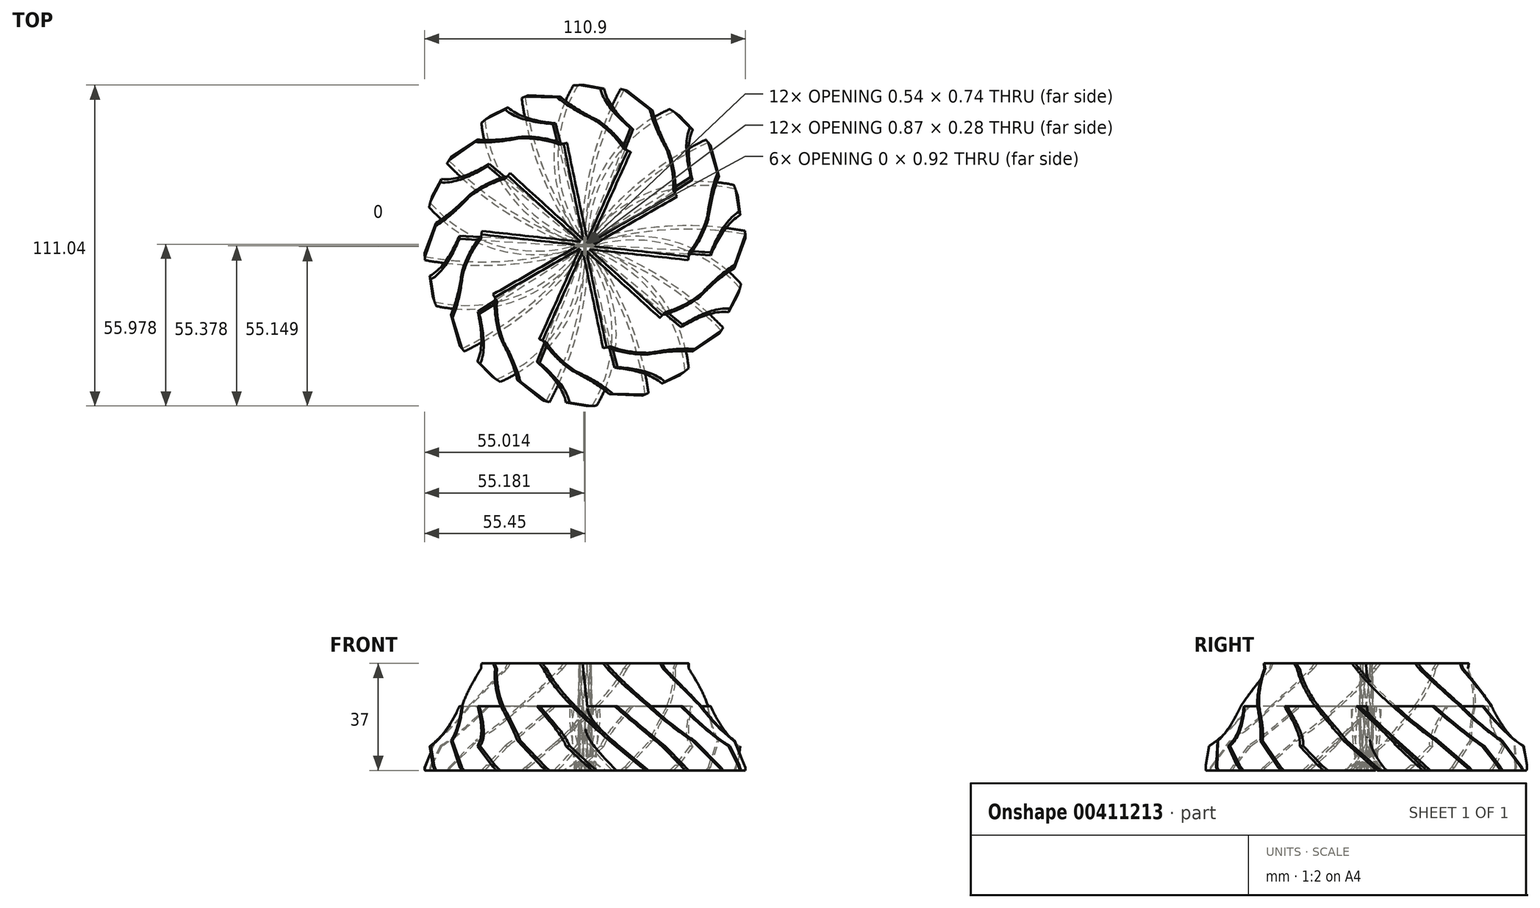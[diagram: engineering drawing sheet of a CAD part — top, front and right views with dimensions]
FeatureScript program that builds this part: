
annotation { "Feature Type Name" : "Feature", "Feature Type Description" : "" }
export const myFeature = defineFeature(function(context is Context, id is Id, definition is map)
    precondition{}
    {
        {
            var Q0;
            Q0=qCreatedBy(makeId("Front.planeOp"),FACE);
            var sketch = newSketch(context, id + "F0", { "sketchPlane" : qUnion([Q0])});
            skLineSegment(sketch, "E0", {"start": v(0, 70) * mm, "end": v(0, -70) * mm, "construction": true});
            skLineSegment(sketch, "E1", {"start": v(0, 0) * mm, "end": v(56, 0) * mm});
            skLineSegment(sketch, "E2", {"start": v(56, 0) * mm, "end": v(56, 1.8) * mm});
            skLineSegment(sketch, "E3", {"start": v(0, 38.2) * mm, "end": v(16, 38.2) * mm});
            skArc(sketch, "E4", {"start": v(16, 38.2) * mm, "mid": v(28.5, 11.77) * mm, "end": v(56, 1.8) * mm});
            skLineSegment(sketch, "E5", {"start": v(16, 0) * mm, "end": v(36, 0) * mm, "construction": true});
            skSolve(sketch);
        }
        {
            var Q0;
            Q0=sQuery(id+"F0.wireOp",EDGE,"E1");
            var Q1;
            Q1=sQuery(id+"F0.wireOp",EDGE,"E4");
            var Q2;
            Q2=sQuery(id+"F0.wireOp",EDGE,"E3");
            var Q3;
            Q3=sQuery(id+"F0.wireOp",EDGE,"E2");
            var Q4;
            Q4=sQuery(id+"F0.wireOp",EDGE,"E0");
            revolve(context, id + "F1", {"bodyType" : ToolBodyType.SURFACE, "surfaceOperationType" : NewSurfaceOperationType.NEW, "surfaceEntities" : qUnion([Q0, Q1, Q2, Q3]), "axis" : qUnion([Q4]), "revolveType" : RevolveType.FULL});
        }
        {
            var Q0;
            Q0=makeQuery(id+"F1.opRevolve","SWEPT_FACE",FACE,{"disambiguationData":[OSD([sQuery(id+"F0.wireOp",EDGE,"E3")])]});
            cPlane(context, id + "F2", {"entities" : qUnion([Q0]), "cplaneType" : CPlaneType.OFFSET, "offset" : (0) * mm, "width" : 150 * mm, "height" : 150 * mm});
        }
        {
            var Q0;
            Q0=qCreatedBy(makeId("Top.planeOp"),FACE);
            var sketch = newSketch(context, id + "F3", { "sketchPlane" : qUnion([Q0])});
            skArc(sketch, "E6", {"start": v(43, 35.88) * mm, "mid": v(19.23, 20.65) * mm, "end": v(0, 0) * mm});
            skArc(sketch, "E7.0", {"start": v(42.2, 36.82) * mm, "mid": v(18.98, 22) * mm, "end": v(0, 2.03) * mm});
            skLineSegment(sketch, "E8", {"start": v(0, 0) * mm, "end": v(0, 2.03) * mm});
            skLineSegment(sketch, "E9", {"start": v(43, 35.88) * mm, "end": v(42.2, 36.82) * mm});
            skSolve(sketch);
        }
        {
            var Q0;
            Q0=qCreatedBy(id+"F2.planeOp",FACE);
            var sketch = newSketch(context, id + "F4", { "sketchPlane" : qUnion([Q0])});
            skLineSegment(sketch, "E10", {"start": v(0, 0) * mm, "end": v(55.5, -7.44) * mm});
            skLineSegment(sketch, "E11", {"start": v(55.5, -7.44) * mm, "end": v(55.34, -8.63) * mm});
            skLineSegment(sketch, "E12", {"start": v(55.34, -8.63) * mm, "end": v(0, -1.21) * mm});
            skLineSegment(sketch, "E13", {"start": v(0, -1.21) * mm, "end": v(0, 0) * mm});
            skLineSegment(sketch, "E14", {"start": v(47.95, -28.93) * mm, "end": v(13.75, -8.3) * mm});
            skLineSegment(sketch, "E15", {"start": v(13.75, -8.3) * mm, "end": v(13.23, -9.15) * mm});
            skLineSegment(sketch, "E16", {"start": v(13.23, -9.15) * mm, "end": v(47.48, -29.81) * mm});
            skLineSegment(sketch, "E17", {"start": v(47.48, -29.81) * mm, "end": v(47.95, -28.93) * mm});
            skCircle(sketch, "E18", {"center": v(55.5, -7.44) * mm, "radius": 22.78 * mm, "construction": true});
            skSolve(sketch);
        }
        {
            var Q0;
            Q0=makeQuery(id+"F1.opRevolve","SWEPT_FACE",FACE,{"disambiguationData":[OSD([sQuery(id+"F0.wireOp",EDGE,"E3")])]});
            cPlane(context, id + "F5", {"entities" : qUnion([Q0]), "cplaneType" : CPlaneType.OFFSET, "offset" : 16 * mm, "oppositeDirection" : true, "width" : 150 * mm, "height" : 150 * mm});
        }
        {
            var Q0;
            Q0=qCreatedBy(makeId("Top.planeOp"),FACE);
            var sketch = newSketch(context, id + "F6", { "sketchPlane" : qUnion([Q0])});
            skArc(sketch, "E19", {"start": v(29.73, 47.35) * mm, "mid": v(7.41, 28.35) * mm, "end": v(0, 0) * mm});
            skLineSegment(sketch, "E20", {"start": v(0, 0) * mm, "end": v(1, 0) * mm});
            skArc(sketch, "E21", {"start": v(31.03, 46.53) * mm, "mid": v(8.78, 27.93) * mm, "end": v(1, 0) * mm});
            skLineSegment(sketch, "E22", {"start": v(29.73, 47.35) * mm, "end": v(31.03, 46.53) * mm});
            skSolve(sketch);
        }
        {
            var Q0;
            Q0=qCreatedBy(id+"F5.planeOp",FACE);
            var sketch = newSketch(context, id + "F7", { "sketchPlane" : qUnion([Q0])});
            skLineSegment(sketch, "E23", {"start": v(1.07, 0) * mm, "end": v(47.4, 29.32) * mm});
            skLineSegment(sketch, "E24", {"start": v(47.4, 29.32) * mm, "end": v(46.88, 30.16) * mm});
            skLineSegment(sketch, "E25", {"start": v(46.88, 30.16) * mm, "end": v(0, 0.5) * mm});
            skLineSegment(sketch, "E26", {"start": v(0, 0.5) * mm, "end": v(1.07, 0) * mm});
            skSolve(sketch);
        }
        {
            var Q0;
            Q0 = qSketchRegion(id + "F3", true);
            var Q1;
            Q1=makeQuery(id+"F4.imprint","IMPRINT",FACE,{"disambiguationData":[TD([[makeQuery(id+"F4.imprint","IMPRINT",EDGE,{"derivedFrom":sQuery(id+"F4.wireOp",EDGE,"E10")}),-1.0]])]});
            loft(context, id + "F8", {"sheetProfilesArray" : [{ "sheetProfileEntities" : qUnion([Q0]) }, { "sheetProfileEntities" : qUnion([Q1]) }]});
        }
        {
            var Q0;
            Q0 = qSketchRegion(id + "F7", true);
            var Q1;
            Q1 = qSketchRegion(id + "F6", true);
            loft(context, id + "F9", {"sheetProfilesArray" : [{ "sheetProfileEntities" : qUnion([Q0]) }, { "sheetProfileEntities" : qUnion([Q1]) }]});
        }
        {
            var Q0;
            Q0=makeQuery(id+"F8.opLoft","SWEPT_BODY",BODY,{"disambiguationData":[OSD([makeQuery(id+"F3.imprint","IMPRINT",FACE,{"disambiguationData":[TD([[makeQuery(id+"F3.imprint","IMPRINT",EDGE,{"derivedFrom":sQuery(id+"F3.wireOp",EDGE,"E6")}),-1.0]])]}),makeQuery(id+"F4.imprint","IMPRINT",FACE,{"disambiguationData":[TD([[makeQuery(id+"F4.imprint","IMPRINT",EDGE,{"derivedFrom":sQuery(id+"F4.wireOp",EDGE,"20717ec0-5c2d-4e27-b742-bf9efb357e74")}),-1.0]])]})])]});
            var Q1;
            Q1=makeQuery(id+"F1.opRevolve","SWEPT_EDGE",EDGE,{"disambiguationData":[OSD([sQuery(id+"F0.wireOp",VERTEX,"E3.end")])]});
            circularPattern(context, id + "F10", {"operationType" : NewBodyOperationType.ADD, "entities" : qUnion([Q0]), "axis" : qUnion([Q1]), "angle" : 360 * degree, "instanceCount" : 10, "equalSpace" : true, "fullFeaturePattern" : false});
        }
        {
            var Q0;
            Q0=makeQuery(id+"F9.opLoft","SWEPT_BODY",BODY,{"disambiguationData":[OSD([makeQuery(id+"F6.imprint","IMPRINT",FACE,{"disambiguationData":[TD([[makeQuery(id+"F6.imprint","IMPRINT",EDGE,{"derivedFrom":sQuery(id+"F6.wireOp",EDGE,"E19")}),1.0]])]}),makeQuery(id+"F7.imprint","IMPRINT",FACE,{"disambiguationData":[TD([[makeQuery(id+"F7.imprint","IMPRINT",EDGE,{"derivedFrom":sQuery(id+"F7.wireOp",EDGE,"E23")}),1.0]])]})])]});
            var Q1;
            Q1=makeQuery(id+"F1.opRevolve","SWEPT_EDGE",EDGE,{"disambiguationData":[OSD([sQuery(id+"F0.wireOp",VERTEX,"E3.end")])]});
            circularPattern(context, id + "F11", {"entities" : qUnion([Q0]), "axis" : qUnion([Q1]), "angle" : 360 * degree, "instanceCount" : 10, "equalSpace" : true});
        }
        {
            var Q0;
            Q0=qCreatedBy(makeId("Front.planeOp"),FACE);
            var sketch = newSketch(context, id + "F12", { "sketchPlane" : qUnion([Q0])});
            skLineSegment(sketch, "E27", {"start": v(0, 0) * mm, "end": v(-55.5, 0) * mm});
            skLineSegment(sketch, "E28", {"start": v(-55.5, 0) * mm, "end": v(-55.57, 7.8) * mm});
            skLineSegment(sketch, "E29", {"start": v(0, 0) * mm, "end": v(0, -15.04) * mm});
            skLineSegment(sketch, "E30", {"start": v(0, -15.04) * mm, "end": v(-98.18, -15.04) * mm});
            skLineSegment(sketch, "E31", {"start": v(-98.18, -15.04) * mm, "end": v(-98.18, 58.54) * mm});
            skLineSegment(sketch, "E32", {"start": v(-98.18, 58.54) * mm, "end": v(0, 58.54) * mm});
            skLineSegment(sketch, "E33", {"start": v(0, 58.54) * mm, "end": v(0, 37) * mm});
            skLineSegment(sketch, "E34", {"start": v(0, 37) * mm, "end": v(-36, 37) * mm});
            skLineSegment(sketch, "E35", {"start": v(-36, 37) * mm, "end": v(-36, 35.2) * mm});
            skLineSegment(sketch, "E36", {"start": v(-36, 35.2) * mm, "end": v(-43.5, 22.2) * mm});
            skArc(sketch, "E37", {"start": v(-55.57, 7.8) * mm, "mid": v(-48.34, 14) * mm, "end": v(-43.5, 22.2) * mm});
            skSolve(sketch);
        }
        {
            var Q0;
            Q0=makeQuery(id+"F12.imprint","IMPRINT",FACE,{"disambiguationData":[TD([[makeQuery(id+"F12.imprint","IMPRINT",EDGE,{"derivedFrom":sQuery(id+"F12.wireOp",EDGE,"E27")}),1.0]])]});
            var Q1;
            Q1=sQuery(id+"F0.wireOp",EDGE,"E0");
            revolve(context, id + "F13", {"operationType" : NewBodyOperationType.REMOVE, "surfaceOperationType" : NewSurfaceOperationType.NEW, "entities" : qUnion([Q0]), "axis" : qUnion([Q1]), "revolveType" : RevolveType.FULL, "oppositeDirection" : true});
        }
    });
